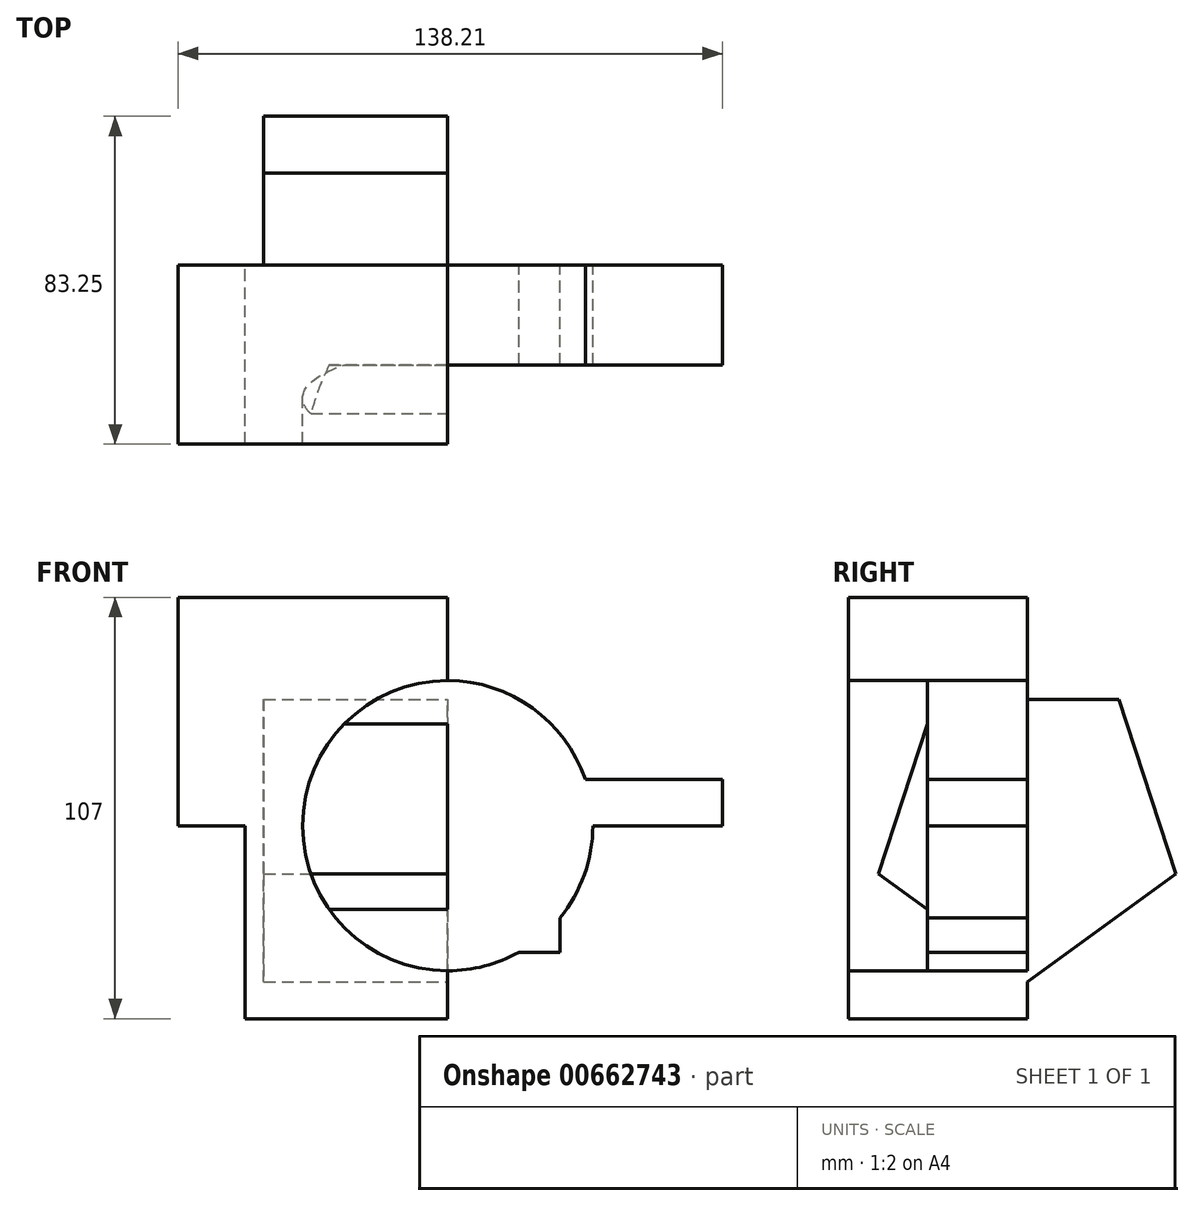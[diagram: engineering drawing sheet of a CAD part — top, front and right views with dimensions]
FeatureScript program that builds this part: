
annotation { "Feature Type Name" : "Feature", "Feature Type Description" : "" }
export const myFeature = defineFeature(function(context is Context, id is Id, definition is map)
    precondition{}
    {
        {
            var Q0;
            Q0=qCreatedBy(makeId("Front.planeOp"),FACE);
            var sketch = newSketch(context, id + "F0", { "sketchPlane" : qUnion([Q0])});
            skCircle(sketch, "E0", {"center": v(0, 0) * mm, "radius": 36.86 * mm});
            skLineSegment(sketch, "E1.bottom", {"start": v(0, 0) * mm, "end": v(-68.46, 0) * mm});
            skLineSegment(sketch, "E1.top", {"start": v(0, 57.98) * mm, "end": v(-68.46, 57.98) * mm});
            skLineSegment(sketch, "E1.left", {"start": v(0, 0) * mm, "end": v(0, 57.98) * mm});
            skLineSegment(sketch, "E1.right", {"start": v(-68.46, 0) * mm, "end": v(-68.46, 57.98) * mm});
            skLineSegment(sketch, "E2.bottom", {"start": v(0, 0) * mm, "end": v(-51.44, 0) * mm});
            skLineSegment(sketch, "E2.top", {"start": v(0, -49.02) * mm, "end": v(-51.44, -49.02) * mm});
            skLineSegment(sketch, "E2.left", {"start": v(0, 0) * mm, "end": v(0, -49.02) * mm});
            skLineSegment(sketch, "E2.right", {"start": v(-51.44, 0) * mm, "end": v(-51.44, -49.02) * mm});
            skLineSegment(sketch, "E3.bottom", {"start": v(0, 0) * mm, "end": v(69.75, 0) * mm});
            skLineSegment(sketch, "E3.top", {"start": v(0, 11.75) * mm, "end": v(69.75, 11.75) * mm});
            skLineSegment(sketch, "E3.left", {"start": v(0, 0) * mm, "end": v(0, 11.75) * mm});
            skLineSegment(sketch, "E3.right", {"start": v(69.75, 0) * mm, "end": v(69.75, 11.75) * mm});
            skLineSegment(sketch, "E4.bottom", {"start": v(0, 0) * mm, "end": v(28.5, 0) * mm});
            skLineSegment(sketch, "E4.top", {"start": v(0, -32.13) * mm, "end": v(28.5, -32.13) * mm});
            skLineSegment(sketch, "E4.left", {"start": v(0, 0) * mm, "end": v(0, -32.13) * mm});
            skLineSegment(sketch, "E4.right", {"start": v(28.5, 0) * mm, "end": v(28.5, -32.13) * mm});
            skSolve(sketch);
        }
        {
            var Q0;
            {var subQ4=sQuery(id+"F0.wireOp",EDGE,"E1.bottom");Q0=makeQuery(id+"F0.imprint","IMPRINT",FACE,{"disambiguationData":[TD([[makeQuery(id+"F0.imprint","IMPRINT",EDGE,{"derivedFrom":subQ4}),-1.0]])]});}
            var Q1;
            {var subQ1=sQuery(id+"F0.wireOp",EDGE,"E2.top");Q1=makeQuery(id+"F0.imprint","IMPRINT",FACE,{"disambiguationData":[TD([[makeQuery(id+"F0.imprint","IMPRINT",EDGE,{"derivedFrom":subQ1}),-1.0]])]});}
            extrude(context, id + "F1", {"entities" : qUnion([Q0, Q1]), "depth" : 45.47 * mm, "offsetDistance" : 25.4 * mm});
        }
        {
            var Q0;
            Q0 = qSketchRegion(id + "F0", true);
            extrude(context, id + "F2", {"entities" : qUnion([Q0]), "operationType" : NewBodyOperationType.ADD, "depth" : 25.4 * mm, "offsetDistance" : 25.4 * mm});
        }
        {
            var Q0;
            Q0=qCreatedBy(makeId("Right.planeOp"),FACE);
            var sketch = newSketch(context, id + "F3", { "sketchPlane" : qUnion([Q0])});
            skCircle(sketch, "E5", {"center": v(0, 0) * mm, "radius": 32.14 * mm});
            skCircle(sketch, "E6.cCircle", {"center": v(0, 0) * mm, "radius": 32.14 * mm, "construction": true});
            skLineSegment(sketch, "E6.0", {"start": v(-23.35, 32.14) * mm, "end": v(23.35, 32.14) * mm});
            skLineSegment(sketch, "E6.1", {"start": v(23.35, 32.14) * mm, "end": v(37.78, -12.28) * mm});
            skLineSegment(sketch, "E6.2", {"start": v(37.78, -12.28) * mm, "end": v(0, -39.73) * mm});
            skLineSegment(sketch, "E6.3", {"start": v(0, -39.73) * mm, "end": v(-37.78, -12.28) * mm});
            skLineSegment(sketch, "E6.4", {"start": v(-37.78, -12.28) * mm, "end": v(-23.35, 32.14) * mm});
            skPoint(sketch, "E6.0.midPoint", {"position": v(0, 32.14) * mm});
            skSolve(sketch);
        }
        {
            var Q0;
            Q0 = qSketchRegion(id + "F3", true);
            extrude(context, id + "F4", {"entities" : qUnion([Q0]), "operationType" : NewBodyOperationType.ADD, "oppositeDirection" : true, "depth" : 46.74 * mm, "offsetDistance" : 25.4 * mm});
        }
    });
